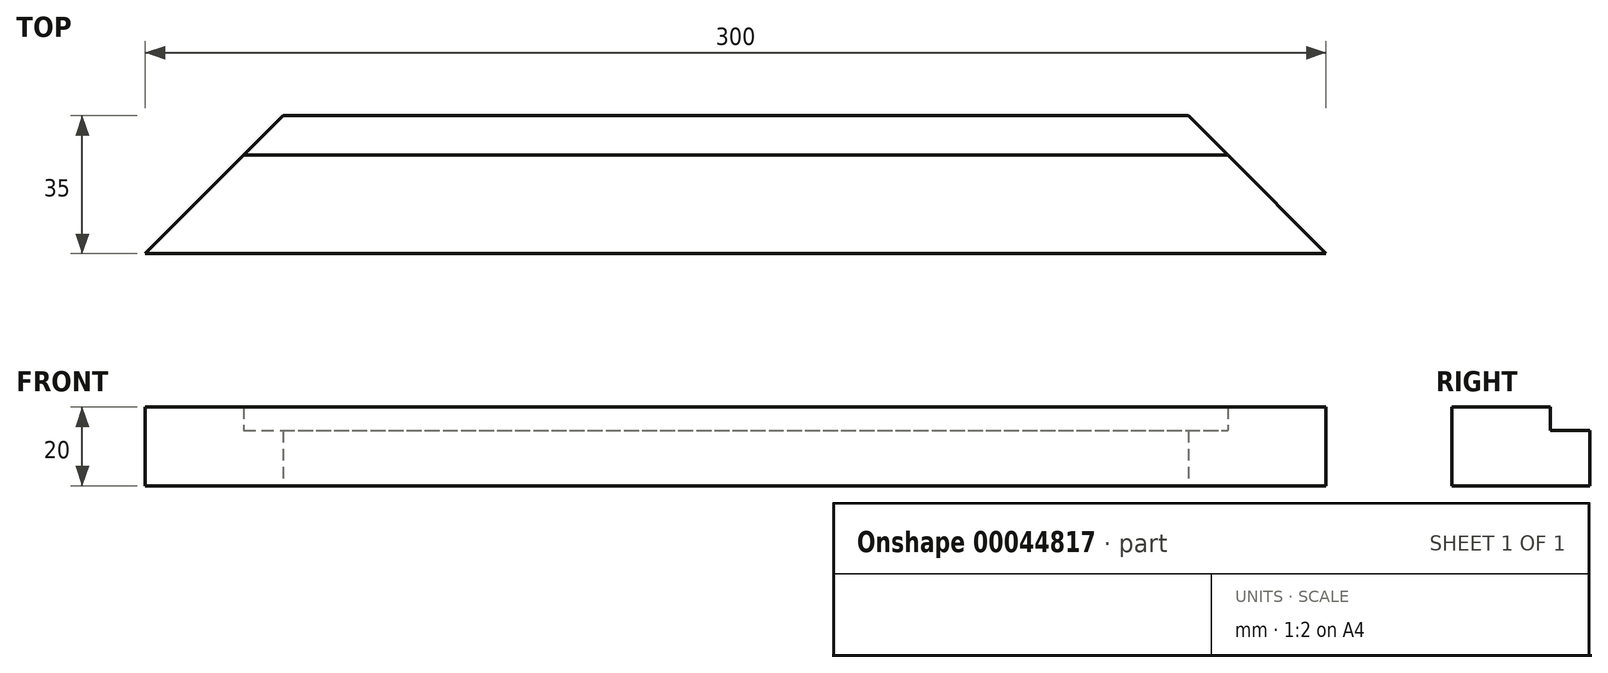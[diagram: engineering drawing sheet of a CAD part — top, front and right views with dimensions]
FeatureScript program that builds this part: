
annotation { "Feature Type Name" : "Feature", "Feature Type Description" : "" }
export const myFeature = defineFeature(function(context is Context, id is Id, definition is map)
    precondition{}
    {
        {
            var Q0;
            Q0=qCreatedBy(makeId("Top.planeOp"),FACE);
            var sketch = newSketch(context, id + "F0", { "sketchPlane" : qUnion([Q0])});
            skLineSegment(sketch, "E0.bottom", {"start": v(-73.7, 24.85) * mm, "end": v(156.3, 24.85) * mm});
            skLineSegment(sketch, "E0.top", {"start": v(-108.7, -10.15) * mm, "end": v(191.3, -10.15) * mm});
            skLineSegment(sketch, "E1", {"start": v(-108.7, -10.15) * mm, "end": v(-73.7, 24.85) * mm});
            skLineSegment(sketch, "E2", {"start": v(156.3, 24.85) * mm, "end": v(191.3, -10.15) * mm});
            skLineSegment(sketch, "E3.trimOffspring", {"start": v(-83.7, 14.85) * mm, "end": v(166.3, 14.85) * mm});
            skPoint(sketch, "E0.left.start.orphan", {"position": v(-108.7, 24.85) * mm});
            skPoint(sketch, "E4.orphan", {"position": v(191.3, 24.85) * mm});
            skPoint(sketch, "E5.orphan", {"position": v(197.05, 14.85) * mm});
            skSolve(sketch);
        }
        {
            var Q0;
            {var subQ0=sQuery(id+"F0.wireOp",EDGE,"E0.bottom");Q0=makeQuery(id+"F0.imprint","IMPRINT",FACE,{"disambiguationData":[TD([[makeQuery(id+"F0.imprint","IMPRINT",EDGE,{"derivedFrom":subQ0}),-1.0]])]});}
            var Q1;
            {var subQ0=sQuery(id+"F0.wireOp",EDGE,"E0.top");Q1=makeQuery(id+"F0.imprint","IMPRINT",FACE,{"disambiguationData":[TD([[makeQuery(id+"F0.imprint","IMPRINT",EDGE,{"derivedFrom":subQ0}),1.0]])]});}
            extrude(context, id + "F1", {"entities" : qUnion([Q0, Q1]), "depth" : 14 * mm});
        }
        {
            var Q0;
            Q0=makeQuery(id+"F1.opExtrude","CAP_FACE",FACE,{"disambiguationData":[OSD([sQuery(id+"F0.wireOp",EDGE,"E0.bottom"),sQuery(id+"F0.wireOp",EDGE,"E0.top"),sQuery(id+"F0.wireOp",EDGE,"E1"),sQuery(id+"F0.wireOp",EDGE,"E2")])],"isStart":false});
            var sketch = newSketch(context, id + "F2", { "sketchPlane" : qUnion([Q0])});
            skLineSegment(sketch, "E6", {"start": v(-107.2, 14.85) * mm, "end": v(212.08, 14.85) * mm});
            skSolve(sketch);
        }
        {
            var Q0;
            {var subQ5=makeQuery(id+"F1.opExtrude","CAP_EDGE",EDGE,{"disambiguationData":[OSD([sQuery(id+"F0.wireOp",EDGE,"E0.top")])],"isStart":false});Q0=makeQuery(id+"F2.imprint","IMPRINT",FACE,{"disambiguationData":[TD([[makeQuery(id+"F2.imprint","IMPRINT",EDGE,{"derivedFrom":subQ5}),1.0]])]});}
            extrude(context, id + "F3", {"entities" : qUnion([Q0]), "operationType" : NewBodyOperationType.ADD, "depth" : 6 * mm});
        }
    });
